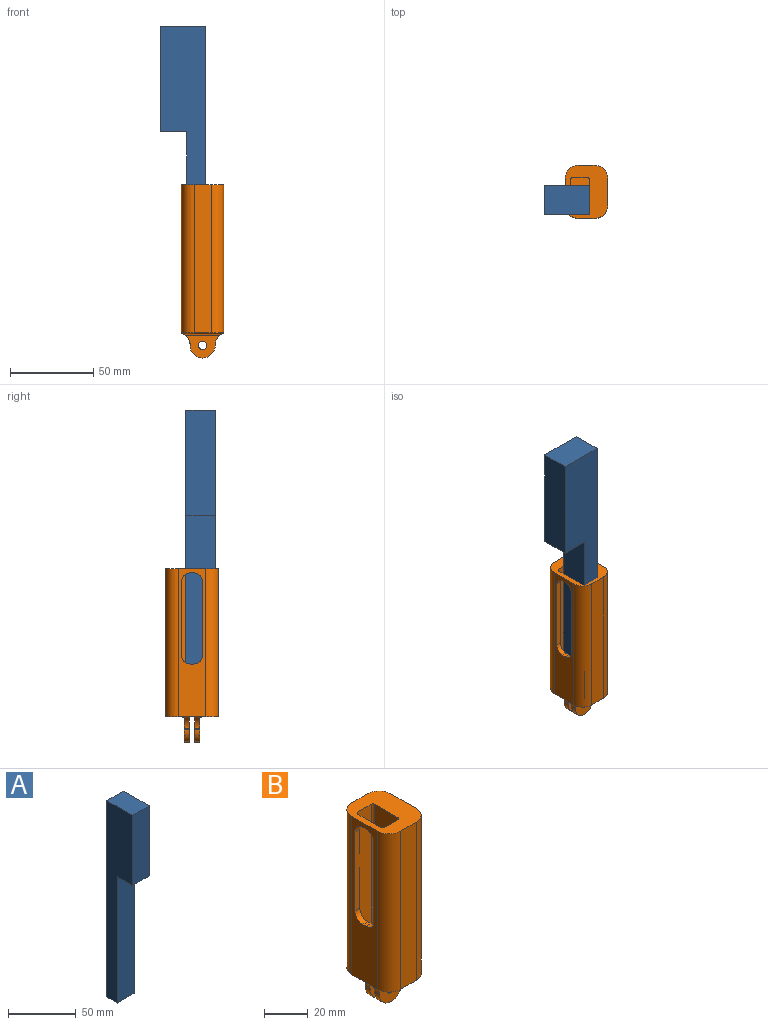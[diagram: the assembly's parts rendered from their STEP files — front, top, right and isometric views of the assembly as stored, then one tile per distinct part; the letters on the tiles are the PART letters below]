
ASSEMBLY  parts=2 mates=1
PART A: 8 faces, bbox 17.5x27x177.8 mm
  f0: plane 114.3x17.46mm, normal (0,-1,0), area 1996mm2, adj f1,f3,f5,f6
  f1: plane 177.8x26.99mm, normal (1,0,0), area 2983.9mm2, adj f0,f2,f4,f5,f6,f7
  f2: plane 177.8x17.46mm, normal (0,1,0), area 3104.8mm2, adj f1,f3,f4,f5
  f3: plane 177.8x26.99mm, normal (-1,0,0), area 2983.9mm2, adj f0,f2,f4,f5,f6,f7
  f4: plane 26.99x17.46mm, normal (0,0,1), area 471.3mm2, adj f1,f2,f3,f7
  f5: plane 17.46x11.11mm, normal (0,0,-1), area 194.1mm2, adj f0,f1,f2,f3
  f6: plane 17.46x15.88mm, normal (0,0,-1), area 277.2mm2, adj f0,f1,f3,f7
  f7: plane 63.5x17.46mm, normal (0,-1,0), area 1108.9mm2, adj f1,f3,f4,f6
PART B: 61 faces, bbox 25.4x31.8x103.9 mm
  f0: plane 11.11x7.17mm, normal (0,0,1), area 79mm2, adj f4,f12,f13,f24,f47,f48
  f1: plane 11.11x3.12mm, normal (0,0,-1), area 34.7mm2, adj f8,f12,f17,f24
  f2: cylinder r=1.91mm len=4.76mm, axis (1,0,0), area 57mm2, adj f8,f40
  f3: plane 88.9x16.51mm, normal (-1,0,0), area 813.7mm2, adj f5,f6,f10,f11,f29,f33,f36,f37
  f4: plane 88.9x14.92mm, normal (1,0,0), area 597.6mm2, adj f0,f5,f10,f15,f17,f24,f36,f37
  f5: plane 3.18x3.12mm, normal (0,0,-1), area 9.9mm2, adj f3,f4,f17,f24
  f6: plane 25.4x10.05mm, normal (0,0,-1), area 230.2mm2, adj f3,f7,f8,f55,f56,f60
  f7: plane 88.9x10.16mm, normal (0,-1,0), area 903.2mm2, adj f6,f10,f55,f56
  f8: plane 88.9x16.51mm, normal (1,0,0), area 1456.3mm2, adj f1,f2,f6,f10,f11,f28,f32,f56
  f9: plane 88.9x10.16mm, normal (0,1,0), area 903.2mm2, adj f10,f11,f57,f58
  f10: plane 31.75x25.4mm, normal (0,0,1), area 563.9mm2, adj f3,f4,f7,f8,f9,f12,f13,f14
  f11: plane 25.4x10.05mm, normal (0,0,-1), area 230.2mm2, adj f3,f8,f9,f57,f58,f59
  f12: plane 88.9x14.92mm, normal (-1,0,0), area 1190.8mm2, adj f0,f1,f10,f15,f17,f24,f41,f42
  f13: plane 82.55x8.57mm, normal (0,-1,0), area 707.7mm2, adj f0,f10,f47,f48
  f14: plane 82.55x8.57mm, normal (0,1,0), area 707.7mm2, adj f10,f15,f49,f50
  f15: plane 11.11x7.17mm, normal (0,0,1), area 79mm2, adj f4,f12,f14,f17,f49,f50
  f16: plane 3x0.53mm, normal (-1,0,0), area 1.6mm2, adj f17,f19,f33,f35
  f17: plane 25.4x21.35mm, normal (0,1,0), area 271.2mm2, adj f1,f4,f5,f12,f15,f16,f18,f20
  f18: plane 3x0.53mm, normal (1,0,0), area 1.6mm2, adj f17,f19,f32,f34
  f19: plane 20.6x13.73mm, normal (0,-1,0), area 171.9mm2, adj f16,f18,f20,f27,f32,f33,f34,f35
  f20: plane 3x0.2mm, normal (0,0,-1), area 0.6mm2, adj f17,f19,f34,f35
  f21: plane 3x0.53mm, normal (-1,0,0), area 1.6mm2, adj f22,f24,f29,f31
  f22: plane 20.6x13.73mm, normal (0,1,0), area 171.9mm2, adj f21,f23,f25,f26,f28,f29,f30,f31
  f23: plane 3x0.53mm, normal (1,0,0), area 1.6mm2, adj f22,f24,f28,f30
  f24: plane 25.4x21.35mm, normal (0,-1,0), area 271.2mm2, adj f0,f1,f4,f5,f12,f21,f23,f25
  f25: plane 3x0.2mm, normal (0,0,-1), area 0.6mm2, adj f22,f24,f30,f31
  f26: cylinder r=2.55mm len=5.1mm, axis (0,-1,0), area 48.1mm2, adj f22,f24
  f27: cylinder r=2.55mm len=5.1mm, axis (0,-1,0), area 48.1mm2, adj f17,f19
  f28: cylinder r=7.4mm len=7.07mm, axis (0,-1,0), area 29.1mm2, adj f8,f22,f23,f24,f59
  f29: cylinder r=7.4mm len=7.07mm, axis (0,-1,0), area 29.1mm2, adj f3,f21,f22,f24,f59
  f30: cylinder r=7.4mm len=7.4mm, axis (0,1,0), area 34.9mm2, adj f22,f23,f24,f25
  f31: cylinder r=7.4mm len=7.4mm, axis (0,-1,0), area 34.9mm2, adj f21,f22,f24,f25
  f32: cylinder r=7.4mm len=7.07mm, axis (0,-1,0), area 29.1mm2, adj f8,f17,f18,f19,f60
  f33: cylinder r=7.4mm len=7.07mm, axis (0,-1,0), area 29.1mm2, adj f3,f16,f17,f19,f60
  f34: cylinder r=7.4mm len=7.4mm, axis (0,1,0), area 34.9mm2, adj f17,f18,f19,f20
  f35: cylinder r=7.4mm len=7.4mm, axis (0,-1,0), area 34.9mm2, adj f16,f17,f19,f20
  f36: plane 3.18x2.22mm, normal (0,0,1), area 7.1mm2, adj f3,f4,f51,f52
  f37: plane 44.45x3.18mm, normal (0,-1,0), area 141.1mm2, adj f3,f4,f51,f53
  f38: plane 44.45x3.18mm, normal (0,1,0), area 141.1mm2, adj f3,f4,f52,f54
  f39: plane 3.18x2.22mm, normal (0,0,-1), area 7.1mm2, adj f3,f4,f53,f54
  f40: plane 9.68x8.38mm, normal (-1,0,0), area 49.4mm2, adj f2,f41,f42,f43,f44,f45,f46
  f41: plane 6.35x4.84mm, normal (0,1,0), area 30.7mm2, adj f12,f40,f42,f46
  f42: plane 6.35x4.19mm, normal (0,0.5,-0.87), area 30.7mm2, adj f12,f40,f41,f43
  f43: plane 6.35x4.19mm, normal (0,-0.5,-0.87), area 30.7mm2, adj f12,f40,f42,f44
  f44: plane 6.35x4.84mm, normal (0,-1,0), area 30.7mm2, adj f12,f40,f43,f45
  f45: plane 6.35x4.19mm, normal (0,-0.5,0.87), area 30.7mm2, adj f12,f40,f44,f46
  f46: plane 6.35x4.19mm, normal (0,0.5,0.87), area 30.7mm2, adj f12,f40,f41,f45
  f47: cylinder r=1.27mm len=82.55mm, axis (0,0,-1), area 164.7mm2, adj f0,f10,f12,f13
  f48: cylinder r=1.27mm len=82.55mm, axis (0,0,1), area 164.7mm2, adj f0,f4,f10,f13
  f49: cylinder r=1.27mm len=82.55mm, axis (0,0,-1), area 164.7mm2, adj f4,f10,f14,f15
  f50: cylinder r=1.27mm len=82.55mm, axis (0,0,1), area 164.7mm2, adj f10,f12,f14,f15
  f51: cylinder r=5.08mm len=5.08mm, axis (1,0,0), area 25.3mm2, adj f3,f4,f36,f37
  f52: cylinder r=5.08mm len=5.08mm, axis (-1,0,0), area 25.3mm2, adj f3,f4,f36,f38
  f53: cylinder r=5.08mm len=5.08mm, axis (-1,0,0), area 25.3mm2, adj f3,f4,f37,f39
  f54: cylinder r=5.08mm len=5.08mm, axis (1,0,0), area 25.3mm2, adj f3,f4,f38,f39
  f55: cylinder r=7.62mm len=88.9mm, axis (0,0,1), area 1064.1mm2, adj f3,f6,f7,f10
  f56: cylinder r=7.62mm len=88.9mm, axis (0,0,-1), area 1064.1mm2, adj f6,f7,f8,f10
  f57: cylinder r=7.62mm len=88.9mm, axis (0,0,1), area 1064.1mm2, adj f8,f9,f10,f11
  f58: cylinder r=7.62mm len=88.9mm, axis (0,0,-1), area 1064.1mm2, adj f3,f9,f10,f11
  f59: cylinder r=1.27mm len=25.4mm, axis (-1,0,0), area 46.6mm2, adj f11,f22,f28,f29
  f60: cylinder r=1.27mm len=25.4mm, axis (1,0,0), area 46.6mm2, adj f6,f19,f32,f33
PLACE A rot(axis=(0,0,-1),90deg) t=(-3.97,-5.12,6.24)mm
PLACE B at identity fixed
MATE slider B.f15 <-> A.f5  axis (0,0,1) through (-3.97,-5.12,6.35)mm
